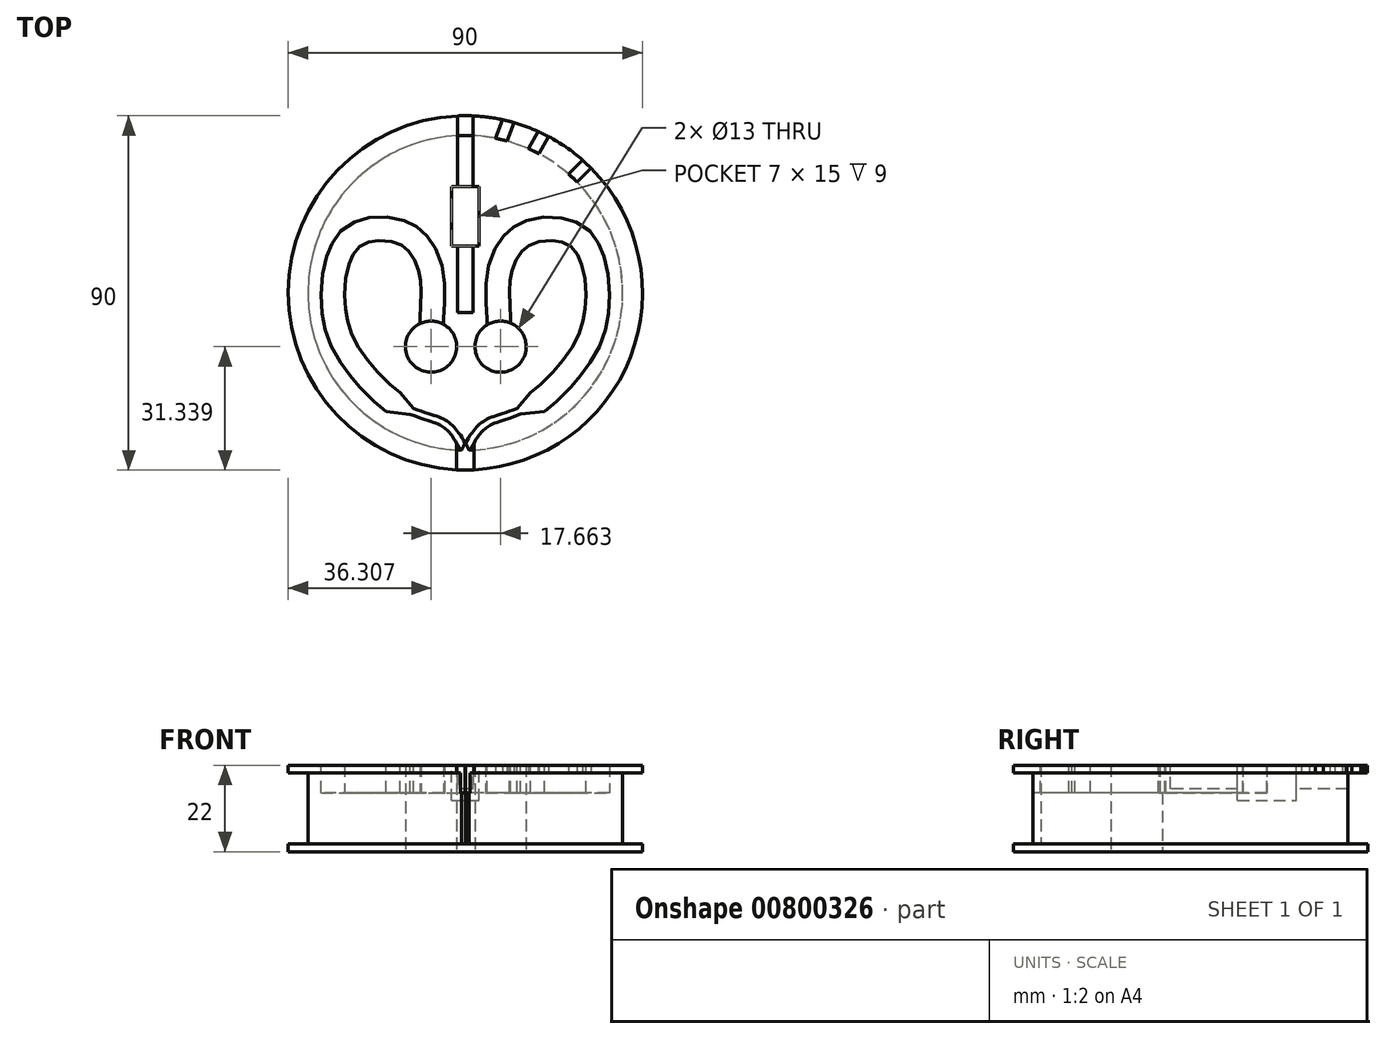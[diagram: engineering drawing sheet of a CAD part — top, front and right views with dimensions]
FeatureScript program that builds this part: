
annotation { "Feature Type Name" : "Feature", "Feature Type Description" : "" }
export const myFeature = defineFeature(function(context is Context, id is Id, definition is map)
    precondition{}
    {
        {
            var Q0;
            Q0=qCreatedBy(makeId("Top.planeOp"),FACE);
            var sketch = newSketch(context, id + "F0", { "sketchPlane" : qUnion([Q0])});
            skCircle(sketch, "E0", {"center": v(0, 0) * mm, "radius": 40 * mm});
            skCircle(sketch, "E1", {"center": v(-8.7, -13.66) * mm, "radius": 6.5 * mm});
            skCircle(sketch, "E2", {"center": v(8.97, -13.66) * mm, "radius": 6.5 * mm});
            skFitSpline(sketch, "E3.0", {"points": [v(-17.88, -26.97) * mm, v(-16.17, -27.8) * mm, v(-13.19, -29.08) * mm, v(-9.8, -30.25) * mm, v(-7.63, -30.94) * mm, v(-6.12, -31.53) * mm, v(-5.06, -32.05) * mm, v(-4.07, -32.7) * mm, v(-3.15, -33.53) * mm, v(-2.3, -34.47) * mm, v(-1.27, -35.85) * mm, v(-0.14, -37.73) * mm, v(0.61, -39.26) * mm, v(0.95, -39.99) * mm]});
            skFitSpline(sketch, "E4.MirrorCS", {"points": [v(17.88, -26.97) * mm, v(16.17, -27.8) * mm, v(13.19, -29.08) * mm, v(9.8, -30.25) * mm, v(7.63, -30.94) * mm, v(6.12, -31.53) * mm, v(5.06, -32.05) * mm, v(4.07, -32.7) * mm, v(3.15, -33.53) * mm, v(2.3, -34.47) * mm, v(1.27, -35.85) * mm, v(0.14, -37.73) * mm, v(-0.61, -39.26) * mm, v(-0.95, -39.99) * mm]});
            skSolve(sketch);
        }
        {
            var Q0;
            Q0=makeQuery(id+"F0.imprint","IMPRINT",FACE,{"disambiguationData":[TD([[makeQuery(id+"F0.imprint","IMPRINT",EDGE,{"derivedFrom":sQuery(id+"F0.wireOp",EDGE,"E2")}),-1.0]])]});
            extrude(context, id + "F1", {"entities" : qUnion([Q0]), "depth" : 22 * mm, "offsetDistance" : 25 * mm});
        }
        {
            var Q0;
            Q0=makeQuery(id+"F1.opExtrude","CAP_FACE",FACE,{"disambiguationData":[OSD([sQuery(id+"F0.wireOp",EDGE,"E0"),sQuery(id+"F0.wireOp",EDGE,"E1"),sQuery(id+"F0.wireOp",EDGE,"E2"),sQuery(id+"F0.wireOp",EDGE,"E3.0"),sQuery(id+"F0.wireOp",EDGE,"E4.MirrorCS")])],"isStart":false});
            var sketch = newSketch(context, id + "F2", { "sketchPlane" : qUnion([Q0])});
            skFitSpline(sketch, "E5.0", {"points": [v(-5.49, -6.49) * mm, v(-5.44, -4.89) * mm, v(-5.26, -2.4) * mm, v(-5.21, 1.17) * mm, v(-5.4, 3.97) * mm, v(-5.92, 6.9) * mm, v(-6.85, 9.81) * mm, v(-8.02, 12.14) * mm, v(-9.24, 13.88) * mm, v(-10.3, 15.1) * mm, v(-11.52, 16.2) * mm, v(-12.92, 17.16) * mm, v(-14.4, 17.91) * mm, v(-16.44, 18.67) * mm, v(-19.07, 19.22) * mm, v(-22.23, 19.34) * mm, v(-24.75, 19.02) * mm, v(-26.66, 18.52) * mm, v(-28.49, 17.83) * mm, v(-30.62, 16.59) * mm, v(-32.39, 14.8) * mm, v(-33.54, 13.1) * mm, v(-34.28, 11.7) * mm, v(-34.9, 10.2) * mm, v(-35.59, 8.08) * mm, v(-36.2, 5.23) * mm, v(-36.58, 1.62) * mm, v(-36.62, -2.07) * mm, v(-36.36, -5.1) * mm, v(-35.97, -7.44) * mm, v(-35.46, -9.69) * mm, v(-34.6, -12.3) * mm, v(-33.26, -15.16) * mm, v(-31.7, -17.76) * mm, v(-30.27, -19.75) * mm, v(-29.08, -21.27) * mm, v(-27.85, -22.76) * mm, v(-26.25, -24.57) * mm, v(-23.59, -27.29) * mm, v(-21.53, -29.09) * mm, v(-20.16, -30.13) * mm]});
            skFitSpline(sketch, "E6.0", {"points": [v(-11.49, -6.3) * mm, v(-11.46, -5.42) * mm, v(-11.37, -3.7) * mm, v(-11.24, -1.27) * mm, v(-11.22, 0.66) * mm, v(-11.3, 2.16) * mm, v(-11.4, 3.26) * mm, v(-11.56, 4.35) * mm, v(-11.8, 5.44) * mm, v(-12.1, 6.5) * mm, v(-12.6, 7.87) * mm, v(-13.23, 9.12) * mm, v(-13.98, 10.19) * mm, v(-14.6, 10.89) * mm, v(-15.26, 11.49) * mm, v(-15.97, 11.98) * mm, v(-16.8, 12.4) * mm, v(-18.04, 12.87) * mm, v(-19.79, 13.24) * mm, v(-21.6, 13.3) * mm, v(-23, 13.19) * mm, v(-23.97, 13.02) * mm, v(-24.85, 12.79) * mm, v(-25.87, 12.4) * mm, v(-26.9, 11.8) * mm, v(-27.75, 10.94) * mm, v(-28.39, 10.01) * mm, v(-28.84, 9.17) * mm, v(-29.26, 8.15) * mm, v(-29.76, 6.59) * mm, v(-30.26, 4.3) * mm, v(-30.58, 1.28) * mm, v(-30.6, -1.34) * mm, v(-30.48, -3.38) * mm, v(-30.32, -4.87) * mm, v(-30.08, -6.28) * mm, v(-29.68, -8.05) * mm, v(-29, -10.08) * mm, v(-27.96, -12.33) * mm, v(-26.7, -14.44) * mm, v(-25.23, -16.5) * mm, v(-23.59, -18.53) * mm, v(-21.85, -20.48) * mm, v(-19.47, -22.91) * mm, v(-17.66, -24.49) * mm, v(-16.51, -25.37) * mm]});
            skFitSpline(sketch, "E7.0", {"points": [v(-18.6, -28.72) * mm, v(-16.86, -29.59) * mm, v(-13.8, -30.93) * mm, v(-10.3, -32.17) * mm, v(-8.16, -32.88) * mm, v(-6.8, -33.42) * mm, v(-5.95, -33.85) * mm, v(-5.32, -34.27) * mm, v(-4.84, -34.68) * mm, v(-4.36, -35.14) * mm, v(-3.78, -35.8) * mm, v(-3.1, -36.72) * mm, v(-2.46, -37.72) * mm, v(-1.67, -39.13) * mm, v(-1.14, -40.22) * mm, v(-0.83, -40.92) * mm]});
            skFitSpline(sketch, "E8.0", {"points": [v(-17.9, -27.25) * mm, v(-16.18, -28.08) * mm, v(-13.2, -29.35) * mm, v(-9.82, -30.53) * mm, v(-7.65, -31.22) * mm, v(-6.13, -31.81) * mm, v(-5.08, -32.33) * mm, v(-4.09, -32.98) * mm, v(-3.16, -33.8) * mm, v(-2.32, -34.75) * mm, v(-1.29, -36.13) * mm, v(-0.16, -38.01) * mm, v(0.6, -39.54) * mm, v(0.93, -40.27) * mm]});
            skLineSegment(sketch, "E9", {"start": v(-11.49, -6.3) * mm, "end": v(-11.49, -8.09) * mm});
            skLineSegment(sketch, "E10", {"start": v(-5.49, -6.49) * mm, "end": v(-5.49, -8.29) * mm});
            skLineSegment(sketch, "E11", {"start": v(-16.51, -25.37) * mm, "end": v(-13.11, -29.34) * mm});
            skLineSegment(sketch, "E12", {"start": v(-20.16, -30.13) * mm, "end": v(-13.8, -30.87) * mm});
            skFitSpline(sketch, "E13.MirrorCS", {"points": [v(18.61, -28.7) * mm, v(16.86, -29.57) * mm, v(13.8, -30.92) * mm, v(10.3, -32.16) * mm, v(8.16, -32.86) * mm, v(6.81, -33.4) * mm, v(5.95, -33.84) * mm, v(5.32, -34.26) * mm, v(4.84, -34.66) * mm, v(4.37, -35.12) * mm, v(3.78, -35.79) * mm, v(3.1, -36.7) * mm, v(2.47, -37.7) * mm, v(1.67, -39.12) * mm, v(1.14, -40.2) * mm, v(0.83, -40.9) * mm]});
            skFitSpline(sketch, "E14.MirrorCS", {"points": [v(17.9, -27.26) * mm, v(16.18, -28.09) * mm, v(13.2, -29.36) * mm, v(9.82, -30.54) * mm, v(7.65, -31.23) * mm, v(6.13, -31.82) * mm, v(5.08, -32.34) * mm, v(4.08, -33) * mm, v(3.16, -33.81) * mm, v(2.32, -34.76) * mm, v(1.29, -36.14) * mm, v(0.15, -38.02) * mm, v(-0.6, -39.55) * mm, v(-0.94, -40.28) * mm]});
            skLineSegment(sketch, "E15.MirrorCS", {"start": v(20.16, -30.14) * mm, "end": v(13.8, -30.86) * mm});
            skLineSegment(sketch, "E16.MirrorCS", {"start": v(16.51, -25.38) * mm, "end": v(13.11, -29.35) * mm});
            skFitSpline(sketch, "E17.MirrorCS", {"points": [v(11.49, -6.3) * mm, v(11.46, -5.43) * mm, v(11.37, -3.72) * mm, v(11.24, -1.28) * mm, v(11.22, 0.65) * mm, v(11.29, 2.15) * mm, v(11.4, 3.25) * mm, v(11.56, 4.34) * mm, v(11.8, 5.43) * mm, v(12.1, 6.5) * mm, v(12.6, 7.86) * mm, v(13.23, 9.11) * mm, v(13.98, 10.18) * mm, v(14.6, 10.88) * mm, v(15.26, 11.48) * mm, v(15.97, 11.97) * mm, v(16.8, 12.4) * mm, v(18.04, 12.86) * mm, v(19.78, 13.23) * mm, v(21.6, 13.3) * mm, v(23, 13.18) * mm, v(23.97, 13.01) * mm, v(24.85, 12.78) * mm, v(25.87, 12.4) * mm, v(26.9, 11.78) * mm, v(27.75, 10.93) * mm, v(28.39, 10) * mm, v(28.84, 9.16) * mm, v(29.26, 8.14) * mm, v(29.76, 6.58) * mm, v(30.26, 4.3) * mm, v(30.58, 1.27) * mm, v(30.6, -1.35) * mm, v(30.48, -3.4) * mm, v(30.32, -4.88) * mm, v(30.08, -6.3) * mm, v(29.68, -8.05) * mm, v(29, -10.1) * mm, v(27.96, -12.34) * mm, v(26.7, -14.45) * mm, v(25.23, -16.5) * mm, v(23.58, -18.54) * mm, v(21.85, -20.49) * mm, v(19.47, -22.92) * mm, v(17.66, -24.5) * mm, v(16.51, -25.38) * mm]});
            skLineSegment(sketch, "E18.MirrorCS", {"start": v(5.49, -6.5) * mm, "end": v(5.49, -8.3) * mm});
            skLineSegment(sketch, "E19.MirrorCS", {"start": v(11.49, -6.3) * mm, "end": v(11.49, -8.1) * mm});
            skFitSpline(sketch, "E20.MirrorCS", {"points": [v(5.49, -6.5) * mm, v(5.44, -4.9) * mm, v(5.26, -2.4) * mm, v(5.21, 1.16) * mm, v(5.4, 3.96) * mm, v(5.92, 6.88) * mm, v(6.85, 9.8) * mm, v(8.02, 12.13) * mm, v(9.24, 13.87) * mm, v(10.3, 15.1) * mm, v(11.52, 16.2) * mm, v(12.92, 17.15) * mm, v(14.4, 17.9) * mm, v(16.44, 18.66) * mm, v(19.07, 19.21) * mm, v(22.23, 19.33) * mm, v(24.75, 19.01) * mm, v(26.65, 18.51) * mm, v(28.49, 17.82) * mm, v(30.62, 16.58) * mm, v(32.39, 14.8) * mm, v(33.54, 13.1) * mm, v(34.28, 11.7) * mm, v(34.9, 10.2) * mm, v(35.58, 8.07) * mm, v(36.2, 5.22) * mm, v(36.58, 1.6) * mm, v(36.62, -2.08) * mm, v(36.36, -5.11) * mm, v(35.97, -7.45) * mm, v(35.46, -9.7) * mm, v(34.6, -12.31) * mm, v(33.26, -15.17) * mm, v(31.7, -17.77) * mm, v(30.27, -19.76) * mm, v(29.08, -21.28) * mm, v(27.85, -22.77) * mm, v(26.25, -24.58) * mm, v(23.59, -27.3) * mm, v(21.53, -29.1) * mm, v(20.16, -30.14) * mm]});
            skLineSegment(sketch, "E21", {"start": v(-11.49, -8.09) * mm, "end": v(-5.49, -8.29) * mm});
            skLineSegment(sketch, "E22", {"start": v(-11.49, -6.3) * mm, "end": v(-5.49, -6.49) * mm});
            skLineSegment(sketch, "E23", {"start": v(-20.16, -30.13) * mm, "end": v(-16.51, -25.37) * mm});
            skLineSegment(sketch, "E24", {"start": v(5.49, -8.3) * mm, "end": v(11.49, -8.1) * mm});
            skLineSegment(sketch, "E25", {"start": v(16.51, -25.38) * mm, "end": v(20.16, -30.14) * mm});
            skLineSegment(sketch, "E26", {"start": v(-13.8, -30.87) * mm, "end": v(-13.11, -29.34) * mm});
            skLineSegment(sketch, "E27", {"start": v(13.11, -29.35) * mm, "end": v(13.8, -30.86) * mm});
            skLineSegment(sketch, "E28", {"start": v(-1.13, -40.27) * mm, "end": v(-0.94, -40.28) * mm});
            skLineSegment(sketch, "E29", {"start": v(0.93, -40.27) * mm, "end": v(1.13, -40.26) * mm});
            skLineSegment(sketch, "E30", {"start": v(0.93, -40.27) * mm, "end": v(-0.94, -40.28) * mm});
            skSolve(sketch);
        }
        {
            var Q0;
            Q0=makeQuery(id+"F2.imprint","IMPRINT",FACE,{"disambiguationData":[TD([[makeQuery(id+"F2.imprint","IMPRINT",EDGE,{"derivedFrom":sQuery(id+"F2.wireOp",EDGE,"E5.0")}),1.0]])]});
            var Q1;
            {var subQ1=sQuery(id+"F2.wireOp",EDGE,"E17.MirrorCS");Q1=makeQuery(id+"F2.imprint","IMPRINT",FACE,{"disambiguationData":[TD([[makeQuery(id+"F2.imprint","IMPRINT",EDGE,{"derivedFrom":subQ1}),1.0]])]});}
            var Q2;
            {var subQ0=sQuery(id+"F2.wireOp",EDGE,"E22");Q2=makeQuery(id+"F2.imprint","IMPRINT",FACE,{"disambiguationData":[TD([[makeQuery(id+"F2.imprint","IMPRINT",EDGE,{"derivedFrom":subQ0}),-1.0]])]});}
            var Q3;
            {var subQ0=sQuery(id+"F2.wireOp",EDGE,"E21");Q3=makeQuery(id+"F2.imprint","IMPRINT",FACE,{"disambiguationData":[TD([[makeQuery(id+"F2.imprint","IMPRINT",EDGE,{"derivedFrom":subQ0}),1.0]])]});}
            var Q4;
            {var subQ5=sQuery(id+"F2.wireOp",EDGE,"E26");Q4=makeQuery(id+"F2.imprint","IMPRINT",FACE,{"disambiguationData":[TD([[makeQuery(id+"F2.imprint","IMPRINT",EDGE,{"derivedFrom":subQ5}),-1.0]])]});}
            var Q5;
            Q5=makeQuery(id+"F2.imprint","IMPRINT",FACE,{"disambiguationData":[TD([[makeQuery(id+"F2.imprint","IMPRINT",EDGE,{"derivedFrom":sQuery(id+"F2.wireOp",EDGE,"E15.MirrorCS")}),-1.0]])]});
            var Q6;
            Q6=makeQuery(id+"F2.imprint","IMPRINT",FACE,{"disambiguationData":[TD([[makeQuery(id+"F2.imprint","IMPRINT",EDGE,{"derivedFrom":sQuery(id+"F2.wireOp",EDGE,"E11")}),-1.0]])]});
            var Q7;
            {var subQ5=sQuery(id+"F2.wireOp",EDGE,"E27");Q7=makeQuery(id+"F2.imprint","IMPRINT",FACE,{"disambiguationData":[TD([[makeQuery(id+"F2.imprint","IMPRINT",EDGE,{"derivedFrom":subQ5}),-1.0]])]});}
            extrude(context, id + "F3", {"entities" : qUnion([Q0, Q1, Q2, Q3, Q4, Q5, Q6, Q7]), "operationType" : NewBodyOperationType.REMOVE, "oppositeDirection" : true, "depth" : 7 * mm, "offsetDistance" : 25 * mm});
        }
        {
            var Q0;
            Q0=makeQuery(id+"F1.opExtrude","CAP_FACE",FACE,{"disambiguationData":[OSD([sQuery(id+"F0.wireOp",EDGE,"E0"),sQuery(id+"F0.wireOp",EDGE,"E1"),sQuery(id+"F0.wireOp",EDGE,"E2"),sQuery(id+"F0.wireOp",EDGE,"E3.0"),sQuery(id+"F0.wireOp",EDGE,"E4.MirrorCS")])],"isStart":false});
            var sketch = newSketch(context, id + "F4", { "sketchPlane" : qUnion([Q0])});
            skLineSegment(sketch, "E31.bottom", {"start": v(2, 51.95) * mm, "end": v(-2, 51.95) * mm});
            skLineSegment(sketch, "E31.top", {"start": v(2, 26.95) * mm, "end": v(-2, 26.95) * mm});
            skLineSegment(sketch, "E31.left", {"start": v(2, 51.95) * mm, "end": v(2, 26.95) * mm});
            skLineSegment(sketch, "E31.right", {"start": v(-2, 51.95) * mm, "end": v(-2, 26.95) * mm});
            skPoint(sketch, "E31.middle", {"position": v(0, 39.45) * mm});
            skLineSegment(sketch, "E32.bottom", {"start": v(-3.5, 11.95) * mm, "end": v(3.5, 11.95) * mm});
            skLineSegment(sketch, "E32.top", {"start": v(-3.5, 26.95) * mm, "end": v(3.5, 26.95) * mm});
            skLineSegment(sketch, "E32.left", {"start": v(-3.5, 11.95) * mm, "end": v(-3.5, 26.95) * mm});
            skLineSegment(sketch, "E32.right", {"start": v(3.5, 11.95) * mm, "end": v(3.5, 26.95) * mm});
            skPoint(sketch, "E32.middle", {"position": v(0, 19.45) * mm});
            skLineSegment(sketch, "E33.bottom", {"start": v(-2, 11.95) * mm, "end": v(2, 11.95) * mm});
            skLineSegment(sketch, "E33.top", {"start": v(-2, -5.05) * mm, "end": v(2, -5.05) * mm});
            skLineSegment(sketch, "E33.left", {"start": v(-2, 11.95) * mm, "end": v(-2, -5.05) * mm});
            skLineSegment(sketch, "E33.right", {"start": v(2, 11.95) * mm, "end": v(2, -5.05) * mm});
            skPoint(sketch, "E33.middle", {"position": v(0, 3.45) * mm});
            skSolve(sketch);
        }
        {
            var Q0;
            {var subQ0=sQuery(id+"F4.wireOp",EDGE,"E31.bottom");Q0=makeQuery(id+"F4.imprint","IMPRINT",FACE,{"disambiguationData":[TD([[makeQuery(id+"F4.imprint","IMPRINT",EDGE,{"derivedFrom":subQ0}),1.0]])]});}
            var Q1;
            {var subQ0=sQuery(id+"F4.wireOp",EDGE,"E32.top");var subQ1=sQuery(id+"F4.wireOp",EDGE,"E31.left");var subQ2=makeQuery(id+"F4.imprint","INTERSECT",VERTEX,{"derivedFrom":[subQ1,subQ0]});Q1=makeQuery(id+"F4.imprint","IMPRINT",FACE,{"disambiguationData":[TD([[makeQuery(id+"F4.imprint","IMPRINT",EDGE,{"disambiguationData":[TD([[subQ2,1.0]])],"derivedFrom":subQ1}),-1.0]])]});}
            extrude(context, id + "F5", {"entities" : qUnion([Q0, Q1]), "operationType" : NewBodyOperationType.REMOVE, "oppositeDirection" : true, "depth" : 6 * mm, "offsetDistance" : 25 * mm});
        }
        {
            var Q0;
            {var subQ5=sQuery(id+"F4.wireOp",EDGE,"E33.top");Q0=makeQuery(id+"F4.imprint","IMPRINT",FACE,{"disambiguationData":[TD([[makeQuery(id+"F4.imprint","IMPRINT",EDGE,{"derivedFrom":subQ5}),1.0]])]});}
            extrude(context, id + "F6", {"entities" : qUnion([Q0]), "operationType" : NewBodyOperationType.REMOVE, "oppositeDirection" : true, "depth" : 6 * mm, "offsetDistance" : 25 * mm});
        }
        {
            var Q0;
            {var subQ3=sQuery(id+"F4.wireOp",EDGE,"E32.left");Q0=makeQuery(id+"F4.imprint","IMPRINT",FACE,{"disambiguationData":[TD([[makeQuery(id+"F4.imprint","IMPRINT",EDGE,{"derivedFrom":subQ3}),-1.0]])]});}
            extrude(context, id + "F7", {"entities" : qUnion([Q0]), "operationType" : NewBodyOperationType.REMOVE, "oppositeDirection" : true, "depth" : 9 * mm, "offsetDistance" : 25 * mm});
        }
        {
            var Q0;
            Q0=qCreatedBy(makeId("Top.planeOp"),FACE);
            var sketch = newSketch(context, id + "F8", { "sketchPlane" : qUnion([Q0])});
            skCircle(sketch, "E34", {"center": v(0, 0) * mm, "radius": 45 * mm});
            skCircle(sketch, "E35", {"center": v(0, 0) * mm, "radius": 40 * mm});
            skSolve(sketch);
        }
        {
            var Q0;
            Q0=makeQuery(id+"F8.imprint","IMPRINT",FACE,{"disambiguationData":[TD([[makeQuery(id+"F8.imprint","IMPRINT",EDGE,{"derivedFrom":sQuery(id+"F8.wireOp",EDGE,"E34")}),1.0]])]});
            extrude(context, id + "F9", {"entities" : qUnion([Q0]), "operationType" : NewBodyOperationType.ADD, "depth" : 2 * mm, "offsetDistance" : 25 * mm});
        }
        {
            var Q0;
            Q0 = qSketchRegion(id + "F8", true);
            extrude(context, id + "F10", {"entities" : qUnion([Q0]), "operationType" : NewBodyOperationType.ADD, "depth" : 22 * mm, "offsetDistance" : 25 * mm, "hasSecondDirection" : true, "secondDirectionOppositeDirection" : false, "secondDirectionDepth" : 20 * mm});
        }
        {
            var Q0;
            {var subQ0=sQuery(id+"F4.wireOp",EDGE,"E31.bottom");Q0=makeQuery(id+"F4.imprint","IMPRINT",FACE,{"disambiguationData":[TD([[makeQuery(id+"F4.imprint","IMPRINT",EDGE,{"derivedFrom":subQ0}),1.0]])]});}
            extrude(context, id + "F11", {"entities" : qUnion([Q0]), "operationType" : NewBodyOperationType.REMOVE, "oppositeDirection" : true, "depth" : 4 * mm, "offsetDistance" : 25 * mm});
        }
        {
            var Q0;
            Q0=makeQuery(id+"F10.boolean.opBoolean","MERGE",FACE,{"derivedFrom":[makeQuery(id+"F1.opExtrude","CAP_FACE",FACE,{"disambiguationData":[OSD([sQuery(id+"F0.wireOp",EDGE,"E0"),sQuery(id+"F0.wireOp",EDGE,"E1"),sQuery(id+"F0.wireOp",EDGE,"E2"),sQuery(id+"F0.wireOp",EDGE,"E3.0"),sQuery(id+"F0.wireOp",EDGE,"E4.MirrorCS")])],"isStart":false}),makeQuery(id+"F10.opExtrude","CAP_FACE",FACE,{"disambiguationData":[OSD([sQuery(id+"F8.wireOp",EDGE,"E34"),sQuery(id+"F8.wireOp",EDGE,"E35")])],"isStart":false})]});
            var sketch = newSketch(context, id + "F12", { "sketchPlane" : qUnion([Q0])});
            skLineSegment(sketch, "E36.bottom", {"start": v(2.18, -38.23) * mm, "end": v(-2.22, -38.23) * mm});
            skLineSegment(sketch, "E36.top", {"start": v(2.18, -45.72) * mm, "end": v(-2.22, -45.72) * mm});
            skLineSegment(sketch, "E36.left", {"start": v(2.18, -38.23) * mm, "end": v(2.18, -45.72) * mm});
            skLineSegment(sketch, "E36.right", {"start": v(-2.22, -38.23) * mm, "end": v(-2.22, -45.72) * mm});
            skSolve(sketch);
        }
        {
            var Q0;
            Q0=makeQuery(id+"F12.imprint","IMPRINT",FACE,{"disambiguationData":[TD([[makeQuery(id+"F12.imprint","IMPRINT",EDGE,{"derivedFrom":sQuery(id+"F12.wireOp",EDGE,"E36.top")}),-1.0]])]});
            var Q1;
            {var subQ5=sQuery(id+"F12.wireOp",EDGE,"E36.right");var subQ6=sQuery(id+"F12.wireOp",EDGE,"E36.bottom");var subQ7=makeQuery(id+"F12.imprint","INTERSECT",VERTEX,{"derivedFrom":[subQ6,subQ5]});Q1=makeQuery(id+"F12.imprint","IMPRINT",FACE,{"disambiguationData":[TD([[makeQuery(id+"F12.imprint","IMPRINT",EDGE,{"disambiguationData":[TD([[subQ7,1.0]])],"derivedFrom":subQ6}),1.0]])]});}
            extrude(context, id + "F13", {"entities" : qUnion([Q0, Q1]), "operationType" : NewBodyOperationType.REMOVE, "depth" : 15 * mm, "offsetDistance" : 25 * mm, "hasSecondDirection" : true, "secondDirectionOppositeDirection" : true, "secondDirectionDepth" : 2 * mm});
        }
        {
            var Q0;
            Q0=qCreatedBy(makeId("Top.planeOp"),FACE);
            var sketch = newSketch(context, id + "F14", { "sketchPlane" : qUnion([Q0])});
            skLineSegment(sketch, "E37.bottom", {"start": v(-1.62, -37.27) * mm, "end": v(1.6, -37.27) * mm});
            skLineSegment(sketch, "E37.top", {"start": v(-1.62, -41.22) * mm, "end": v(1.6, -41.22) * mm});
            skLineSegment(sketch, "E37.left", {"start": v(-1.62, -37.27) * mm, "end": v(-1.62, -41.22) * mm});
            skLineSegment(sketch, "E37.right", {"start": v(1.6, -37.27) * mm, "end": v(1.6, -41.22) * mm});
            skSolve(sketch);
        }
        {
            var Q0;
            Q0 = qSketchRegion(id + "F14", true);
            extrude(context, id + "F15", {"entities" : qUnion([Q0]), "operationType" : NewBodyOperationType.ADD, "depth" : 2 * mm, "offsetDistance" : 25 * mm});
        }
        {
            var Q0;
            Q0=makeQuery(id+"F15.boolean.opBoolean","MERGE",FACE,{"derivedFrom":[makeQuery(id+"F9.opExtrude","CAP_FACE",FACE,{"disambiguationData":[OSD([sQuery(id+"F8.wireOp",EDGE,"E34"),sQuery(id+"F8.wireOp",EDGE,"E35")])],"isStart":false}),makeQuery(id+"F15.opExtrude","CAP_FACE",FACE,{"disambiguationData":[OSD([sQuery(id+"F14.wireOp",EDGE,"E37.bottom"),sQuery(id+"F14.wireOp",EDGE,"E37.top"),sQuery(id+"F14.wireOp",EDGE,"E37.left"),sQuery(id+"F14.wireOp",EDGE,"E37.right")])],"isStart":false})]});
            var sketch = newSketch(context, id + "F16", { "sketchPlane" : qUnion([Q0])});
            skLineSegment(sketch, "E38", {"start": v(10.59, 38.57) * mm, "end": v(12.84, 44.36) * mm});
            skLineSegment(sketch, "E39.0", {"start": v(7.63, 39.26) * mm, "end": v(9.9, 45.1) * mm});
            skLineSegment(sketch, "E40", {"start": v(18.72, 35.35) * mm, "end": v(21.74, 40.68) * mm});
            skLineSegment(sketch, "E41", {"start": v(28.38, 28.2) * mm, "end": v(32.6, 32.4) * mm});
            skLineSegment(sketch, "E42.0", {"start": v(16, 36.66) * mm, "end": v(19.04, 42) * mm});
            skLineSegment(sketch, "E43.0", {"start": v(26.18, 30.24) * mm, "end": v(30.42, 34.47) * mm});
            skLineSegment(sketch, "E44", {"start": v(7.63, 39.26) * mm, "end": v(10.59, 38.57) * mm});
            skLineSegment(sketch, "E45", {"start": v(16, 36.66) * mm, "end": v(18.72, 35.35) * mm});
            skLineSegment(sketch, "E46", {"start": v(26.18, 30.24) * mm, "end": v(28.38, 28.2) * mm});
            skLineSegment(sketch, "E47", {"start": v(9.9, 45.1) * mm, "end": v(12.84, 44.36) * mm});
            skLineSegment(sketch, "E48", {"start": v(19.04, 42) * mm, "end": v(21.74, 40.68) * mm});
            skLineSegment(sketch, "E49", {"start": v(30.42, 34.47) * mm, "end": v(32.6, 32.4) * mm});
            skSolve(sketch);
        }
        {
            var Q0;
            Q0 = qSketchRegion(id + "F16", true);
            extrude(context, id + "F17", {"entities" : qUnion([Q0]), "operationType" : NewBodyOperationType.REMOVE, "depth" : 22 * mm, "offsetDistance" : 25 * mm, "hasSecondDirection" : true, "secondDirectionOppositeDirection" : false, "secondDirectionDepth" : 18 * mm});
        }
    });
